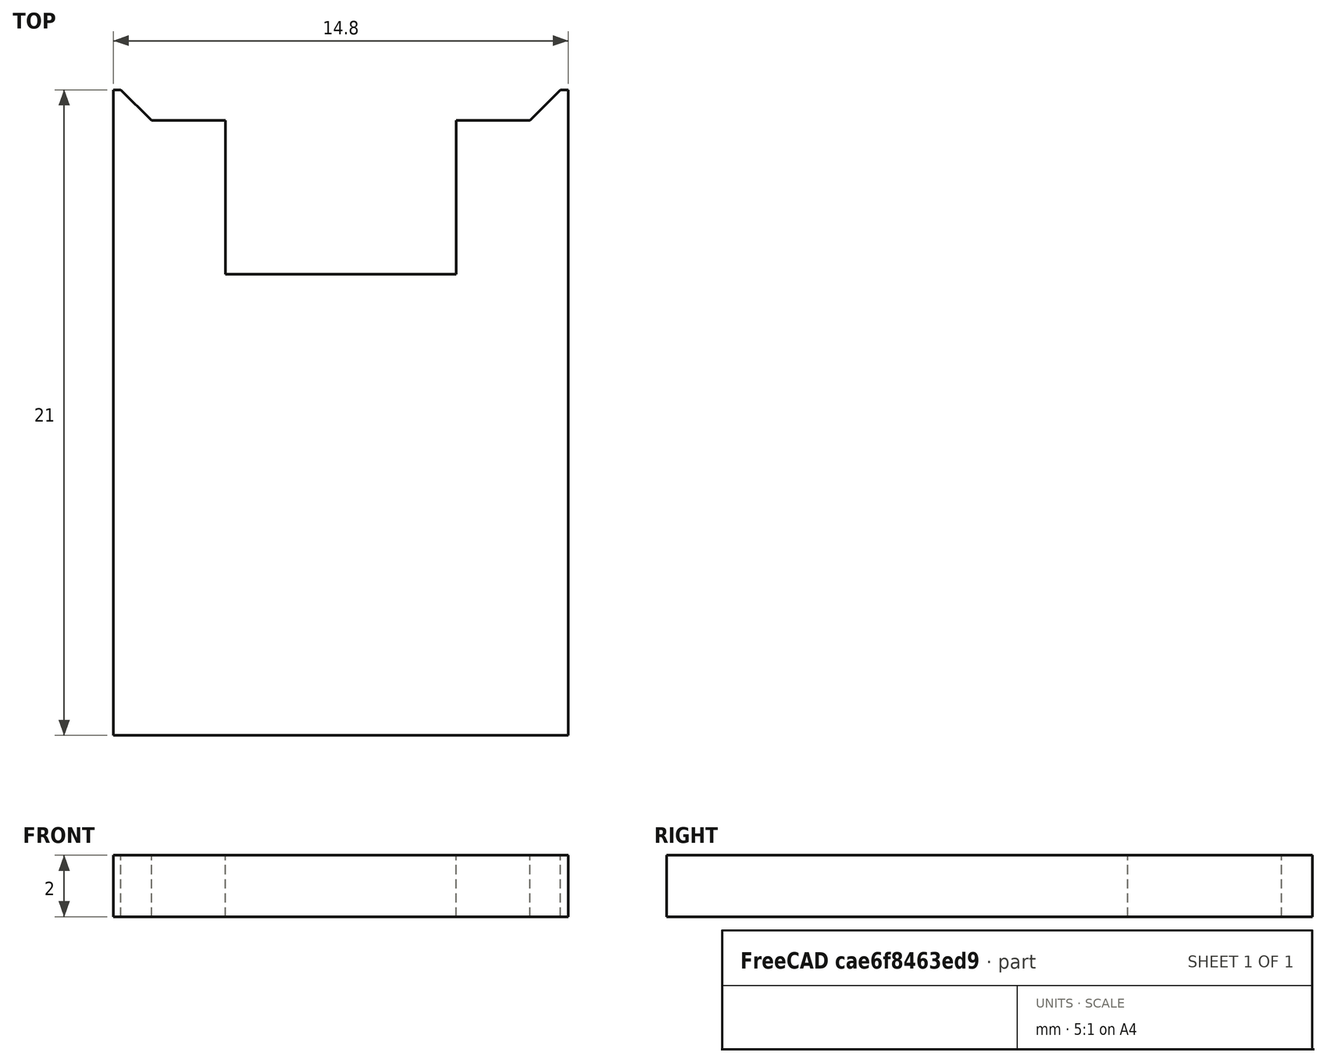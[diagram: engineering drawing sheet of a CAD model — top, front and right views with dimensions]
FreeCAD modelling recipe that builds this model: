
FCSTD DOCUMENT  (FreeCAD 0.19R)
Label: upper tool stage 2 14.8mm
License: All rights reserved
LicenseURL: http://en.wikipedia.org/wiki/All_rights_reserved
objects: Sketcher::SketchObject×1, Part::Extrusion×1
note: 2 computed .brp shape members not serialized (recipe doc carries the construction recipe); baked Part::Feature solids carry a one-line shape summary decoded from their .brp

FEATURE [Sketcher::SketchObject] Sketch
  FullyConstrained = true
  sketch-geometry (12):
    g0: LineSegment StartX=-7.4 StartY=0 StartZ=0 EndX=7.4 EndY=0 EndZ=0
    g1: LineSegment StartX=7.4 StartY=0 StartZ=0 EndX=7.4 EndY=21 EndZ=0
    g2: LineSegment StartX=6.15 StartY=20 StartZ=0 EndX=3.75 EndY=20 EndZ=0
    g3: LineSegment StartX=3.75 StartY=20 StartZ=0 EndX=3.75 EndY=15 EndZ=0
    g4: LineSegment StartX=3.75 StartY=15 StartZ=0 EndX=-3.75 EndY=15 EndZ=0
    g5: LineSegment StartX=-3.75 StartY=15 StartZ=0 EndX=-3.75 EndY=20 EndZ=0
    g6: LineSegment StartX=-3.75 StartY=20 StartZ=0 EndX=-6.15 EndY=20 EndZ=0
    g7: LineSegment StartX=-6.15 StartY=20 StartZ=0 EndX=-7.15 EndY=21 EndZ=0
    g8: LineSegment StartX=-7.15 StartY=21 StartZ=0 EndX=-7.4 EndY=21 EndZ=0
    g9: LineSegment StartX=-7.4 StartY=21 StartZ=0 EndX=-7.4 EndY=0 EndZ=0
    g10: LineSegment StartX=6.15 StartY=20 StartZ=0 EndX=7.15 EndY=21 EndZ=0
    g11: LineSegment StartX=7.15 StartY=21 StartZ=0 EndX=7.4 EndY=21 EndZ=0
  constraints (31):
    c: PointOnObject(g0,g-1)
    c: Coincident(g0,g1)
    c: Vertical(g1)
    c: Horizontal(g2)
    c: Coincident(g2,g3)
    c: Vertical(g3)
    c: Coincident(g3,g4)
    c: Coincident(g4,g5)
    c: Coincident(g5,g6)
    c: Coincident(g6,g7)
    c: Coincident(g7,g8)
    c: Horizontal(g8)
    c: Coincident(g8,g9)
    c: Coincident(g9,g0)
    c: Vertical(g9)
    c: Symmetric(g0,g0,g-2)
    c: Symmetric(g4,g3,g-2)
    c: Symmetric(g5,g2,g-2)
    c: Distance(g0) = 14.8
    c: DistanceY(g0,g3) = 15
    c: Distance(g2) = 2.4
    c: Distance(g4) = 7.5
    c: Coincident(g10,g2)
    c: Coincident(g11,g10)
    c: Coincident(g11,g1)
    c: Horizontal(g11)
    c: Angle(g10,g2) = 2.35619
    c: DistanceY(g6,g7) = 1
    c: Symmetric(g7,g10,g-2)
    c: Symmetric(g6,g2,g-2)
    c: Distance(g5) = 5
FEATURE [Part::Extrusion] Extrude
  Base = -> Sketch
  Dir = (0,0,1)
  DirMode = 2
  FaceMakerClass = Part::FaceMakerBullseye
  LengthFwd = 2
  LengthRev = 0
  Solid = true
  Symmetric = false
